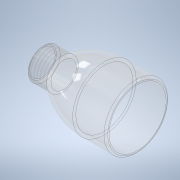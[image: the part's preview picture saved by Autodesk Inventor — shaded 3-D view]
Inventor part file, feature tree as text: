
AUTODESK INVENTOR PART (.ipt)
format: ipt  version: 2021 (Build 250183000, 183)  size: 195,584 bytes
history: native  units: mm
features: thicken_offset x1, thread x1, fillet x1, sketch x1, other x1, revolve x1
ambient origin geometry x8: Origin, YZ Plane, XZ Plane, XY Plane, X Axis, Y Axis, Z Axis, Center Point
bodies: Solid1 (feature_tree)
feature tree (6):
  thicken_offset  "Thicken1"
  thread  "Thread1"  [1 undecoded]
  fillet  "Fillet1"  Radius=10.0mm
  sketch  "Sketch1"  dims[d2=10.0mm d3=90.0deg d4=15.0mm d5=0.5mm d6=0.5mm d7=160.0mm d8=0.0mm d9=0.3mm]
  other  "Srf1"
  revolve  "RevolutionSrf1"  Angle=90.0deg
note: 1 required parameter value undecoded (feature->parameter linkage not recoverable at this tier; creation-order binding heuristic only, values carry confidence <= 0.55)
